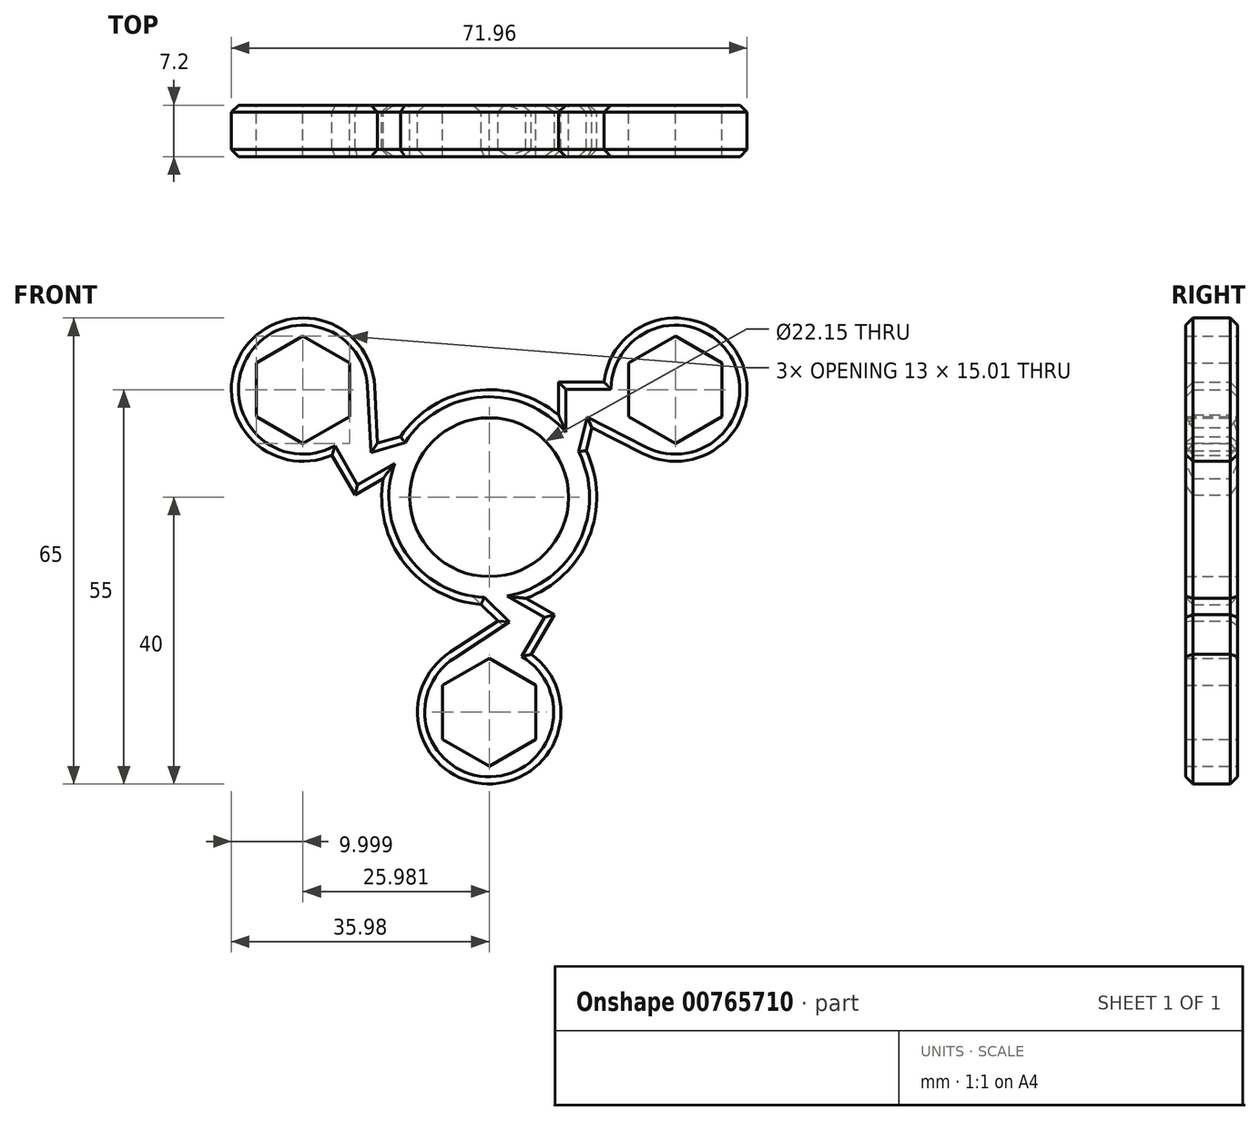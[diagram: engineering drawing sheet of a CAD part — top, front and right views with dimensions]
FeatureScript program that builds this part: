
annotation { "Feature Type Name" : "Feature", "Feature Type Description" : "" }
export const myFeature = defineFeature(function(context is Context, id is Id, definition is map)
    precondition{}
    {
        {
            var Q0;
            Q0=qCreatedBy(makeId("Front.planeOp"),FACE);
            var sketch = newSketch(context, id + "F0", { "sketchPlane" : qUnion([Q0])});
            skCircle(sketch, "E0", {"center": v(0, 0) * mm, "radius": 11.08 * mm});
            skCircle(sketch, "E1", {"center": v(0, 0) * mm, "radius": 40 * mm, "construction": true});
            skArc(sketch, "E2", {"start": v(-14.77, 2.63) * mm, "mid": v(-11.86, -9.19) * mm, "end": v(-1.14, -14.96) * mm});
            skCircle(sketch, "E3.cCircle", {"center": v(0, -30) * mm, "radius": 6.5 * mm, "construction": true});
            skLineSegment(sketch, "E3.0", {"start": v(6.5, -26.25) * mm, "end": v(6.5, -33.75) * mm});
            skLineSegment(sketch, "E3.1", {"start": v(6.5, -33.75) * mm, "end": v(0, -37.5) * mm});
            skLineSegment(sketch, "E3.2", {"start": v(0, -37.5) * mm, "end": v(-6.5, -33.75) * mm});
            skLineSegment(sketch, "E3.3", {"start": v(-6.5, -33.75) * mm, "end": v(-6.5, -26.25) * mm});
            skLineSegment(sketch, "E3.4", {"start": v(-6.5, -26.25) * mm, "end": v(0, -22.5) * mm});
            skLineSegment(sketch, "E3.5", {"start": v(0, -22.5) * mm, "end": v(6.5, -26.25) * mm});
            skPoint(sketch, "E3.0.midPoint", {"position": v(6.5, -30) * mm});
            skArc(sketch, "E4", {"start": v(-5.44, -21.6) * mm, "mid": v(-0.27, -40) * mm, "end": v(5.89, -21.92) * mm});
            skArc(sketch, "E5.1.0", {"start": v(21.44, 6.1) * mm, "mid": v(34.77, 19.76) * mm, "end": v(16.04, 16.06) * mm});
            skLineSegment(sketch, "E5.1.1", {"start": v(32.48, 18.75) * mm, "end": v(32.48, 11.25) * mm});
            skLineSegment(sketch, "E5.1.2", {"start": v(25.98, 22.5) * mm, "end": v(32.48, 18.75) * mm});
            skLineSegment(sketch, "E5.1.3", {"start": v(19.48, 18.75) * mm, "end": v(25.98, 22.5) * mm});
            skLineSegment(sketch, "E5.1.4", {"start": v(19.48, 11.25) * mm, "end": v(19.48, 18.75) * mm});
            skLineSegment(sketch, "E5.1.5", {"start": v(25.98, 7.5) * mm, "end": v(19.48, 11.25) * mm});
            skLineSegment(sketch, "E5.1.6", {"start": v(32.48, 11.25) * mm, "end": v(25.98, 7.5) * mm});
            skArc(sketch, "E5.2.0", {"start": v(-16, 15.52) * mm, "mid": v(-34.5, 20.23) * mm, "end": v(-21.93, 5.86) * mm});
            skLineSegment(sketch, "E5.2.1", {"start": v(-32.48, 18.75) * mm, "end": v(-25.98, 22.5) * mm});
            skLineSegment(sketch, "E5.2.2", {"start": v(-32.48, 11.25) * mm, "end": v(-32.48, 18.75) * mm});
            skLineSegment(sketch, "E5.2.3", {"start": v(-25.98, 7.5) * mm, "end": v(-32.48, 11.25) * mm});
            skLineSegment(sketch, "E5.2.4", {"start": v(-19.48, 11.25) * mm, "end": v(-25.98, 7.5) * mm});
            skLineSegment(sketch, "E5.2.5", {"start": v(-19.48, 18.75) * mm, "end": v(-19.48, 11.25) * mm});
            skLineSegment(sketch, "E5.2.6", {"start": v(-25.98, 22.5) * mm, "end": v(-19.48, 18.75) * mm});
            skLineSegment(sketch, "E6", {"start": v(-5.44, -21.6) * mm, "end": v(1.25, -17.27) * mm});
            skLineSegment(sketch, "E7", {"start": v(1.25, -17.27) * mm, "end": v(-1.14, -14.96) * mm});
            skLineSegment(sketch, "E8", {"start": v(5.89, -21.92) * mm, "end": v(9.07, -16.4) * mm});
            skLineSegment(sketch, "E9", {"start": v(9.07, -16.4) * mm, "end": v(5.1, -14.1) * mm});
            skLineSegment(sketch, "E10.1.0", {"start": v(9.66, 16.06) * mm, "end": v(9.66, 11.47) * mm});
            skLineSegment(sketch, "E10.1.1", {"start": v(16.04, 16.06) * mm, "end": v(9.66, 16.06) * mm});
            skLineSegment(sketch, "E10.1.2", {"start": v(14.34, 9.72) * mm, "end": v(13.52, 6.49) * mm});
            skLineSegment(sketch, "E10.1.3", {"start": v(21.44, 6.1) * mm, "end": v(14.34, 9.72) * mm});
            skLineSegment(sketch, "E10.2.0", {"start": v(-18.74, 0.34) * mm, "end": v(-14.77, 2.63) * mm});
            skLineSegment(sketch, "E10.2.1", {"start": v(-21.93, 5.86) * mm, "end": v(-18.74, 0.34) * mm});
            skLineSegment(sketch, "E10.2.2", {"start": v(-15.58, 7.56) * mm, "end": v(-12.38, 8.47) * mm});
            skLineSegment(sketch, "E10.2.3", {"start": v(-16, 15.52) * mm, "end": v(-15.58, 7.56) * mm});
            skArc(sketch, "E11.trimOffspring", {"start": v(9.66, 11.47) * mm, "mid": v(-2.03, 14.86) * mm, "end": v(-12.38, 8.47) * mm});
            skArc(sketch, "E12.trimOffspring", {"start": v(5.1, -14.1) * mm, "mid": v(13.88, -5.68) * mm, "end": v(13.52, 6.49) * mm});
            skSolve(sketch);
        }
        {
            var Q0;
            Q0 = qSketchRegion(id + "F0", true);
            extrude(context, id + "F1", {"entities" : qUnion([Q0]), "endBound" : BoundingType.SYMMETRIC, "depth" : 7.2 * mm, "offsetDistance" : 25 * mm});
        }
        {
            var Q0;
            Q0=makeQuery(id+"F1.opExtrude","CAP_EDGE",EDGE,{"disambiguationData":[OSD([sQuery(id+"F0.wireOp",EDGE,"E5.2.0")])],"isStart":false});
            var Q1;
            Q1=makeQuery(id+"F1.opExtrude","CAP_EDGE",EDGE,{"disambiguationData":[OSD([sQuery(id+"F0.wireOp",EDGE,"E10.2.1")])],"isStart":false});
            var Q2;
            Q2=makeQuery(id+"F1.opExtrude","CAP_EDGE",EDGE,{"disambiguationData":[OSD([sQuery(id+"F0.wireOp",EDGE,"E10.2.0")])],"isStart":false});
            var Q3;
            Q3=makeQuery(id+"F1.opExtrude","CAP_EDGE",EDGE,{"disambiguationData":[OSD([sQuery(id+"F0.wireOp",EDGE,"E10.2.2")])],"isStart":false});
            var Q4;
            Q4=makeQuery(id+"F1.opExtrude","CAP_EDGE",EDGE,{"disambiguationData":[OSD([sQuery(id+"F0.wireOp",EDGE,"E11.trimOffspring")])],"isStart":false});
            var Q5;
            Q5=makeQuery(id+"F1.opExtrude","CAP_EDGE",EDGE,{"disambiguationData":[OSD([sQuery(id+"F0.wireOp",EDGE,"E2")])],"isStart":false});
            var Q6;
            Q6=makeQuery(id+"F1.opExtrude","CAP_EDGE",EDGE,{"disambiguationData":[OSD([sQuery(id+"F0.wireOp",EDGE,"E12.trimOffspring")])],"isStart":false});
            var Q7;
            Q7=makeQuery(id+"F1.opExtrude","CAP_EDGE",EDGE,{"disambiguationData":[OSD([sQuery(id+"F0.wireOp",EDGE,"E9")])],"isStart":false});
            var Q8;
            Q8=makeQuery(id+"F1.opExtrude","CAP_EDGE",EDGE,{"disambiguationData":[OSD([sQuery(id+"F0.wireOp",EDGE,"E7")])],"isStart":false});
            var Q9;
            Q9=makeQuery(id+"F1.opExtrude","CAP_EDGE",EDGE,{"disambiguationData":[OSD([sQuery(id+"F0.wireOp",EDGE,"E6")])],"isStart":false});
            var Q10;
            Q10=makeQuery(id+"F1.opExtrude","CAP_EDGE",EDGE,{"disambiguationData":[OSD([sQuery(id+"F0.wireOp",EDGE,"E8")])],"isStart":false});
            var Q11;
            Q11=makeQuery(id+"F1.opExtrude","CAP_EDGE",EDGE,{"disambiguationData":[OSD([sQuery(id+"F0.wireOp",EDGE,"E10.1.2")])],"isStart":false});
            var Q12;
            Q12=makeQuery(id+"F1.opExtrude","CAP_EDGE",EDGE,{"disambiguationData":[OSD([sQuery(id+"F0.wireOp",EDGE,"E10.1.3")])],"isStart":false});
            var Q13;
            Q13=makeQuery(id+"F1.opExtrude","CAP_EDGE",EDGE,{"disambiguationData":[OSD([sQuery(id+"F0.wireOp",EDGE,"E10.1.1")])],"isStart":false});
            var Q14;
            Q14=makeQuery(id+"F1.opExtrude","CAP_EDGE",EDGE,{"disambiguationData":[OSD([sQuery(id+"F0.wireOp",EDGE,"E10.1.0")])],"isStart":false});
            chamfer(context, id + "F2", {"entities" : qUnion([Q0, Q1, Q2, Q3, Q4, Q5, Q6, Q7, Q8, Q9, Q10, Q11, Q12, Q13, Q14]), "width" : 1 * mm, "tangentPropagation" : true});
        }
        {
            var Q0;
            Q0=makeQuery(id+"F1.opExtrude","CAP_EDGE",EDGE,{"disambiguationData":[OSD([sQuery(id+"F0.wireOp",EDGE,"E5.2.0")])],"isStart":true});
            var Q1;
            Q1=makeQuery(id+"F1.opExtrude","CAP_EDGE",EDGE,{"disambiguationData":[OSD([sQuery(id+"F0.wireOp",EDGE,"E10.2.3")])],"isStart":true});
            var Q2;
            Q2=makeQuery(id+"F1.opExtrude","CAP_EDGE",EDGE,{"disambiguationData":[OSD([sQuery(id+"F0.wireOp",EDGE,"E10.2.1")])],"isStart":true});
            var Q3;
            Q3=makeQuery(id+"F1.opExtrude","CAP_EDGE",EDGE,{"disambiguationData":[OSD([sQuery(id+"F0.wireOp",EDGE,"E10.2.0")])],"isStart":true});
            var Q4;
            Q4=makeQuery(id+"F1.opExtrude","CAP_EDGE",EDGE,{"disambiguationData":[OSD([sQuery(id+"F0.wireOp",EDGE,"E2")])],"isStart":true});
            var Q5;
            Q5=makeQuery(id+"F1.opExtrude","CAP_EDGE",EDGE,{"disambiguationData":[OSD([sQuery(id+"F0.wireOp",EDGE,"E10.2.2")])],"isStart":true});
            var Q6;
            Q6=makeQuery(id+"F1.opExtrude","CAP_EDGE",EDGE,{"disambiguationData":[OSD([sQuery(id+"F0.wireOp",EDGE,"E11.trimOffspring")])],"isStart":true});
            var Q7;
            Q7=makeQuery(id+"F1.opExtrude","CAP_EDGE",EDGE,{"disambiguationData":[OSD([sQuery(id+"F0.wireOp",EDGE,"E6")])],"isStart":true});
            var Q8;
            Q8=makeQuery(id+"F1.opExtrude","CAP_EDGE",EDGE,{"disambiguationData":[OSD([sQuery(id+"F0.wireOp",EDGE,"E4")])],"isStart":true});
            var Q9;
            Q9=makeQuery(id+"F1.opExtrude","CAP_EDGE",EDGE,{"disambiguationData":[OSD([sQuery(id+"F0.wireOp",EDGE,"E8")])],"isStart":true});
            var Q10;
            Q10=makeQuery(id+"F1.opExtrude","CAP_EDGE",EDGE,{"disambiguationData":[OSD([sQuery(id+"F0.wireOp",EDGE,"E12.trimOffspring")])],"isStart":true});
            var Q11;
            Q11=makeQuery(id+"F1.opExtrude","CAP_EDGE",EDGE,{"disambiguationData":[OSD([sQuery(id+"F0.wireOp",EDGE,"E10.1.2")])],"isStart":true});
            var Q12;
            Q12=makeQuery(id+"F1.opExtrude","CAP_EDGE",EDGE,{"disambiguationData":[OSD([sQuery(id+"F0.wireOp",EDGE,"E10.1.0")])],"isStart":true});
            var Q13;
            Q13=makeQuery(id+"F1.opExtrude","CAP_EDGE",EDGE,{"disambiguationData":[OSD([sQuery(id+"F0.wireOp",EDGE,"E10.1.1")])],"isStart":true});
            var Q14;
            Q14=makeQuery(id+"F1.opExtrude","CAP_EDGE",EDGE,{"disambiguationData":[OSD([sQuery(id+"F0.wireOp",EDGE,"E5.1.0")])],"isStart":true});
            var Q15;
            Q15=makeQuery(id+"F1.opExtrude","CAP_EDGE",EDGE,{"disambiguationData":[OSD([sQuery(id+"F0.wireOp",EDGE,"E10.1.3")])],"isStart":true});
            var Q16;
            Q16=makeQuery(id+"F1.opExtrude","CAP_EDGE",EDGE,{"disambiguationData":[OSD([sQuery(id+"F0.wireOp",EDGE,"E9")])],"isStart":true});
            chamfer(context, id + "F3", {"entities" : qUnion([Q0, Q1, Q2, Q3, Q4, Q5, Q6, Q7, Q8, Q9, Q10, Q11, Q12, Q13, Q14, Q15, Q16]), "width" : 1 * mm, "tangentPropagation" : true});
        }
    });
